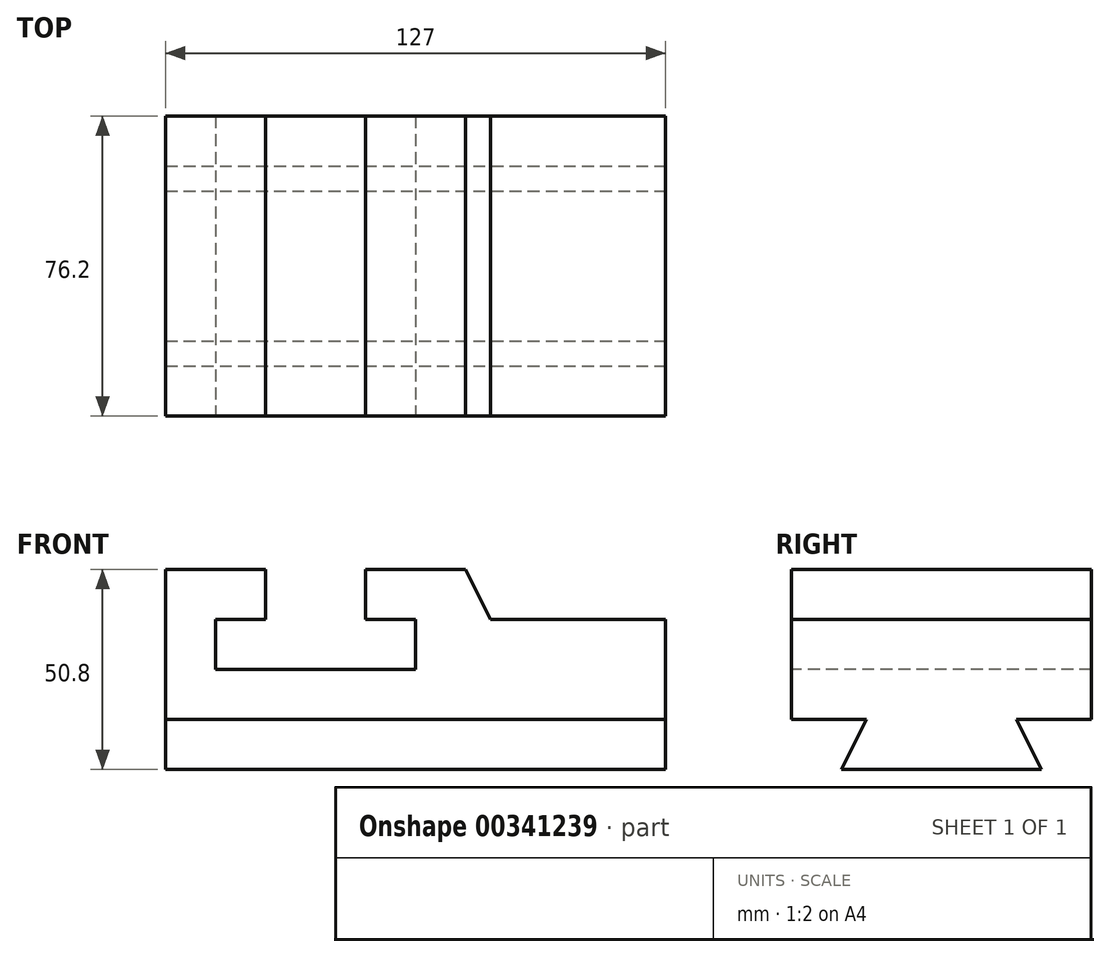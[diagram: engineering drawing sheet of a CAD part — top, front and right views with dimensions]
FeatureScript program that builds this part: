
annotation { "Feature Type Name" : "Feature", "Feature Type Description" : "" }
export const myFeature = defineFeature(function(context is Context, id is Id, definition is map)
    precondition{}
    {
        {
            var Q0;
            Q0=qCreatedBy(makeId("Front.planeOp"),FACE);
            var sketch = newSketch(context, id + "F0", { "sketchPlane" : qUnion([Q0])});
            skLineSegment(sketch, "E0.bottom", {"start": v(0, 0) * mm, "end": v(127, 0) * mm});
            skLineSegment(sketch, "E0.top", {"start": v(0, 50.8) * mm, "end": v(127, 50.8) * mm});
            skLineSegment(sketch, "E0.left", {"start": v(0, 0) * mm, "end": v(0, 50.8) * mm});
            skLineSegment(sketch, "E0.right", {"start": v(127, 0) * mm, "end": v(127, 50.8) * mm});
            skSolve(sketch);
        }
        {
            var Q0;
            Q0 = qSketchRegion(id + "F0", true);
            extrude(context, id + "F1", {"entities" : qUnion([Q0]), "depth" : 76.2 * mm});
        }
        {
            var Q0;
            Q0=makeQuery(id+"F1.opExtrude","CAP_FACE",FACE,{"disambiguationData":[OSD([sQuery(id+"F0.wireOp",EDGE,"E0.bottom"),sQuery(id+"F0.wireOp",EDGE,"E0.top"),sQuery(id+"F0.wireOp",EDGE,"E0.left"),sQuery(id+"F0.wireOp",EDGE,"E0.right")])],"isStart":false});
            var sketch = newSketch(context, id + "F2", { "sketchPlane" : qUnion([Q0])});
            skLineSegment(sketch, "E1.bottom", {"start": v(12.7, 25.4) * mm, "end": v(63.5, 25.4) * mm});
            skLineSegment(sketch, "E1.top", {"start": v(12.7, 38.1) * mm, "end": v(63.5, 38.1) * mm});
            skLineSegment(sketch, "E1.left", {"start": v(12.7, 25.4) * mm, "end": v(12.7, 38.1) * mm});
            skLineSegment(sketch, "E1.right", {"start": v(63.5, 25.4) * mm, "end": v(63.5, 38.1) * mm});
            skLineSegment(sketch, "E2.bottom", {"start": v(25.4, 38.1) * mm, "end": v(50.8, 38.1) * mm});
            skLineSegment(sketch, "E2.top", {"start": v(25.4, 50.8) * mm, "end": v(50.8, 50.8) * mm});
            skLineSegment(sketch, "E2.left", {"start": v(25.4, 38.1) * mm, "end": v(25.4, 50.8) * mm});
            skLineSegment(sketch, "E2.right", {"start": v(50.8, 38.1) * mm, "end": v(50.8, 50.8) * mm});
            skSolve(sketch);
        }
        {
            var Q0;
            Q0 = qSketchRegion(id + "F2", true);
            extrude(context, id + "F3", {"entities" : qUnion([Q0]), "operationType" : NewBodyOperationType.REMOVE, "oppositeDirection" : true, "depth" : 76.2 * mm});
        }
        {
            var Q0;
            Q0=makeQuery(id+"F1.opExtrude","CAP_FACE",FACE,{"disambiguationData":[OSD([sQuery(id+"F0.wireOp",EDGE,"E0.bottom"),sQuery(id+"F0.wireOp",EDGE,"E0.top"),sQuery(id+"F0.wireOp",EDGE,"E0.left"),sQuery(id+"F0.wireOp",EDGE,"E0.right")])],"isStart":false});
            var sketch = newSketch(context, id + "F4", { "sketchPlane" : qUnion([Q0])});
            skLineSegment(sketch, "E3", {"start": v(76.2, 50.8) * mm, "end": v(82.55, 38.1) * mm});
            skLineSegment(sketch, "E4", {"start": v(82.55, 38.1) * mm, "end": v(127, 38.1) * mm});
            skLineSegment(sketch, "E5", {"start": v(127, 38.1) * mm, "end": v(127, 50.8) * mm});
            skLineSegment(sketch, "E6", {"start": v(127, 50.8) * mm, "end": v(76.2, 50.8) * mm});
            skSolve(sketch);
        }
        {
            var Q0;
            Q0 = qSketchRegion(id + "F4", true);
            extrude(context, id + "F5", {"entities" : qUnion([Q0]), "operationType" : NewBodyOperationType.REMOVE, "oppositeDirection" : true, "depth" : 76.2 * mm});
        }
        {
            var Q0;
            Q0=makeQuery(id+"F1.opExtrude","SWEPT_FACE",FACE,{"disambiguationData":[OSD([sQuery(id+"F0.wireOp",EDGE,"E0.right")])]});
            var sketch = newSketch(context, id + "F6", { "sketchPlane" : qUnion([Q0])});
            skLineSegment(sketch, "E7", {"start": v(-76.2, 12.7) * mm, "end": v(-57.15, 12.7) * mm});
            skLineSegment(sketch, "E8", {"start": v(-57.15, 12.7) * mm, "end": v(-63.5, 0) * mm});
            skLineSegment(sketch, "E9", {"start": v(-63.5, 0) * mm, "end": v(-76.2, 0) * mm});
            skLineSegment(sketch, "E10", {"start": v(-76.2, 0) * mm, "end": v(-76.2, 12.7) * mm});
            skLineSegment(sketch, "E11", {"start": v(0, 12.7) * mm, "end": v(-19.05, 12.7) * mm});
            skLineSegment(sketch, "E12", {"start": v(-19.05, 12.7) * mm, "end": v(-12.7, 0) * mm});
            skLineSegment(sketch, "E13", {"start": v(-12.7, 0) * mm, "end": v(0, 0) * mm});
            skLineSegment(sketch, "E14", {"start": v(0, 0) * mm, "end": v(0, 12.7) * mm});
            skSolve(sketch);
        }
        {
            var Q0;
            Q0 = qSketchRegion(id + "F6", true);
            extrude(context, id + "F7", {"entities" : qUnion([Q0]), "operationType" : NewBodyOperationType.REMOVE, "oppositeDirection" : true, "depth" : 127 * mm});
        }
    });
